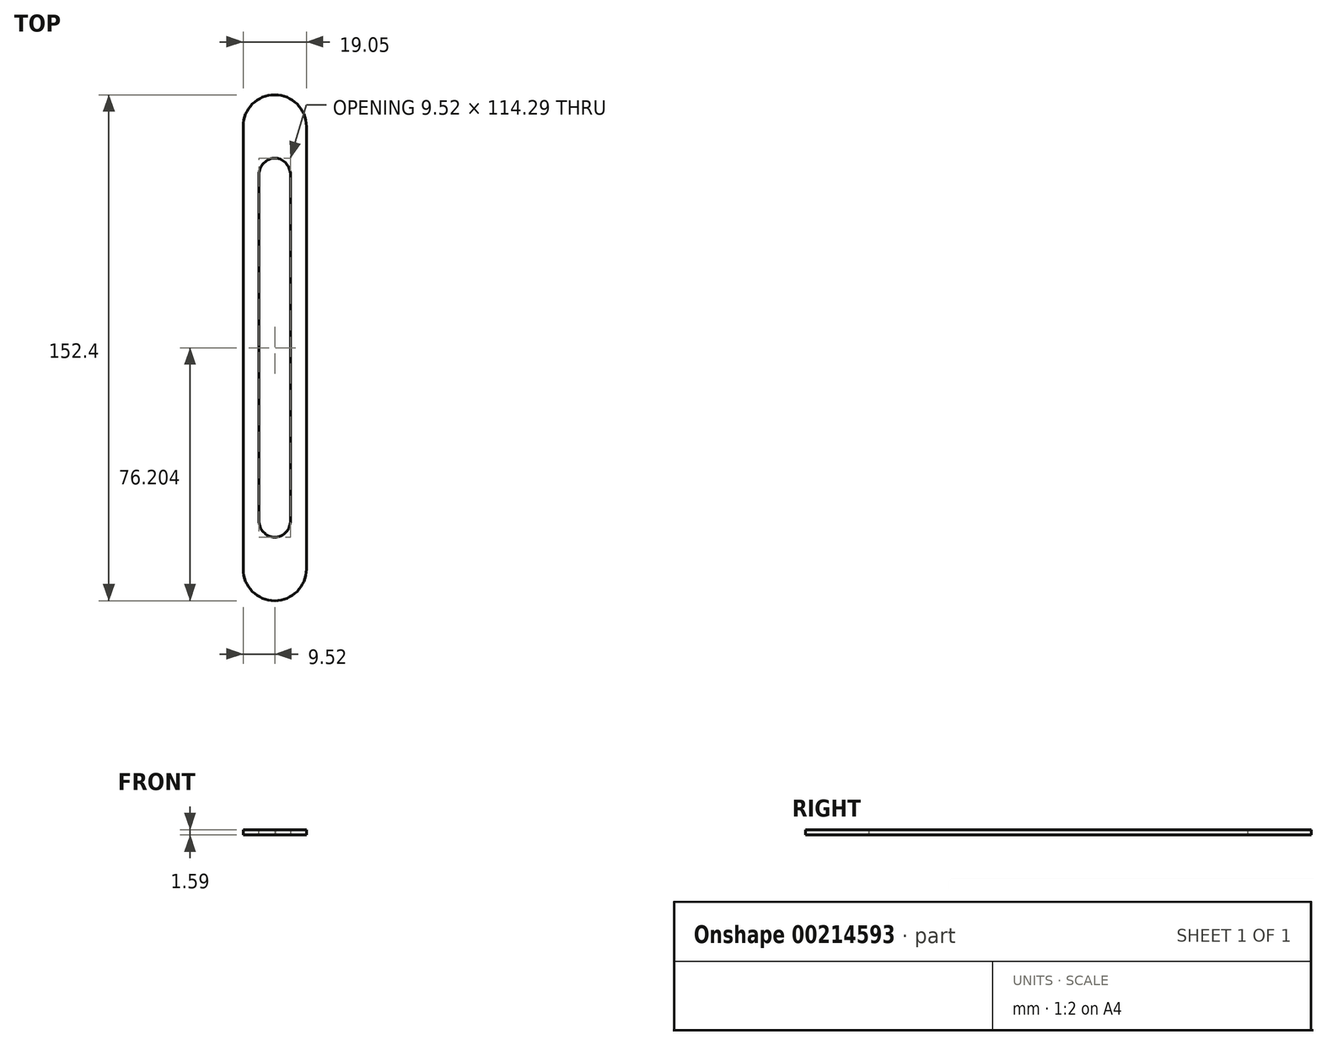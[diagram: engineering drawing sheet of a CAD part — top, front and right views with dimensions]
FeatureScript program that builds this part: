
annotation { "Feature Type Name" : "Feature", "Feature Type Description" : "" }
export const myFeature = defineFeature(function(context is Context, id is Id, definition is map)
    precondition{}
    {
        {
            var Q0;
            Q0=qCreatedBy(makeId("Top.planeOp"),FACE);
            var sketch = newSketch(context, id + "F0", { "sketchPlane" : qUnion([Q0])});
            skLineSegment(sketch, "E0.bottom", {"start": v(-67.62, -47.2) * mm, "end": v(-48.57, -47.2) * mm});
            skLineSegment(sketch, "E0.top", {"start": v(-67.62, 105.2) * mm, "end": v(-48.57, 105.2) * mm});
            skLineSegment(sketch, "E0.left", {"start": v(-67.62, -47.2) * mm, "end": v(-67.62, 105.2) * mm});
            skLineSegment(sketch, "E0.right", {"start": v(-48.57, -47.2) * mm, "end": v(-48.57, 105.2) * mm});
            skSolve(sketch);
        }
        {
            var Q0;
            Q0=makeQuery(id+"F0.imprint","IMPRINT",FACE,{"disambiguationData":[TD([[makeQuery(id+"F0.imprint","IMPRINT",EDGE,{"derivedFrom":sQuery(id+"F0.wireOp",EDGE,"E0.bottom")}),1.0]])]});
            extrude(context, id + "F1", {"entities" : qUnion([Q0]), "oppositeDirection" : true, "depth" : 1.59 * mm});
        }
        {
            var Q0;
            Q0=makeQuery(id+"F1.opExtrude","SWEPT_EDGE",EDGE,{"disambiguationData":[OSD([sQuery(id+"F0.wireOp",EDGE,"E0.bottom"),sQuery(id+"F0.wireOp",EDGE,"E0.right")])]});
            var Q1;
            Q1=makeQuery(id+"F1.opExtrude","SWEPT_EDGE",EDGE,{"disambiguationData":[OSD([sQuery(id+"F0.wireOp",EDGE,"E0.bottom"),sQuery(id+"F0.wireOp",EDGE,"E0.left")])]});
            var Q2;
            Q2=makeQuery(id+"F1.opExtrude","SWEPT_EDGE",EDGE,{"disambiguationData":[OSD([sQuery(id+"F0.wireOp",EDGE,"E0.top"),sQuery(id+"F0.wireOp",EDGE,"E0.right")])]});
            var Q3;
            Q3=makeQuery(id+"F1.opExtrude","SWEPT_EDGE",EDGE,{"disambiguationData":[OSD([sQuery(id+"F0.wireOp",EDGE,"E0.top"),sQuery(id+"F0.wireOp",EDGE,"E0.left")])]});
            fillet(context, id + "F2", {"entities" : qUnion([Q0, Q1, Q2, Q3]), "radius" : 9.52 * mm, "tangentPropagation" : true, "allowEdgeOverflow" : false});
        }
        {
            var Q0;
            Q0=makeQuery(id+"F1.opExtrude","CAP_FACE",FACE,{"disambiguationData":[OSD([sQuery(id+"F0.wireOp",EDGE,"E0.bottom"),sQuery(id+"F0.wireOp",EDGE,"E0.top"),sQuery(id+"F0.wireOp",EDGE,"E0.left"),sQuery(id+"F0.wireOp",EDGE,"E0.right")])],"isStart":true});
            cPlane(context, id + "F3", {"entities" : qUnion([Q0]), "cplaneType" : CPlaneType.OFFSET, "offset" : 0 * mm, "width" : 152.4 * mm, "height" : 152.4 * mm});
        }
        {
            var Q0;
            Q0=qCreatedBy(id+"F3.planeOp",FACE);
            var sketch = newSketch(context, id + "F4", { "sketchPlane" : qUnion([Q0])});
            skLineSegment(sketch, "E1.bottom", {"start": v(-62.86, 86.15) * mm, "end": v(-53.34, 86.15) * mm});
            skLineSegment(sketch, "E1.top", {"start": v(-62.86, -28.15) * mm, "end": v(-53.34, -28.15) * mm});
            skLineSegment(sketch, "E1.left", {"start": v(-62.86, 86.15) * mm, "end": v(-62.86, -28.15) * mm});
            skLineSegment(sketch, "E1.right", {"start": v(-53.34, 86.15) * mm, "end": v(-53.34, -28.15) * mm});
            skSolve(sketch);
        }
        {
            var Q0;
            Q0=makeQuery(id+"F4.imprint","IMPRINT",FACE,{"disambiguationData":[TD([[makeQuery(id+"F4.imprint","IMPRINT",EDGE,{"derivedFrom":sQuery(id+"F4.wireOp",EDGE,"E1.bottom")}),-1.0]])]});
            extrude(context, id + "F5", {"entities" : qUnion([Q0]), "operationType" : NewBodyOperationType.REMOVE, "oppositeDirection" : true, "depth" : 25.4 * mm});
        }
        {
            var Q0;
            Q0=makeQuery(id+"F5.boolean.opBoolean","COPY",EDGE,{"derivedFrom":makeQuery(id+"F5.opExtrude","SWEPT_EDGE",EDGE,{"disambiguationData":[OSD([sQuery(id+"F4.wireOp",EDGE,"E1.top"),sQuery(id+"F4.wireOp",EDGE,"E1.left")])]})});
            var Q1;
            Q1=makeQuery(id+"F5.boolean.opBoolean","COPY",EDGE,{"derivedFrom":makeQuery(id+"F5.opExtrude","SWEPT_EDGE",EDGE,{"disambiguationData":[OSD([sQuery(id+"F4.wireOp",EDGE,"E1.bottom"),sQuery(id+"F4.wireOp",EDGE,"E1.left")])]})});
            var Q2;
            Q2=makeQuery(id+"F5.boolean.opBoolean","COPY",EDGE,{"derivedFrom":makeQuery(id+"F5.opExtrude","SWEPT_EDGE",EDGE,{"disambiguationData":[OSD([sQuery(id+"F4.wireOp",EDGE,"E1.top"),sQuery(id+"F4.wireOp",EDGE,"E1.right")])]})});
            fillet(context, id + "F6", {"entities" : qUnion([Q0, Q1, Q2]), "radius" : 5.08 * mm, "tangentPropagation" : true, "allowEdgeOverflow" : false});
        }
        {
            var Q0;
            Q0=makeQuery(id+"F5.boolean.opBoolean","COPY",EDGE,{"derivedFrom":makeQuery(id+"F5.opExtrude","SWEPT_EDGE",EDGE,{"disambiguationData":[OSD([sQuery(id+"F4.wireOp",EDGE,"E1.bottom"),sQuery(id+"F4.wireOp",EDGE,"E1.right")])]})});
            fillet(context, id + "F7", {"entities" : qUnion([Q0]), "radius" : 5.08 * mm, "tangentPropagation" : true, "allowEdgeOverflow" : false});
        }
    });
